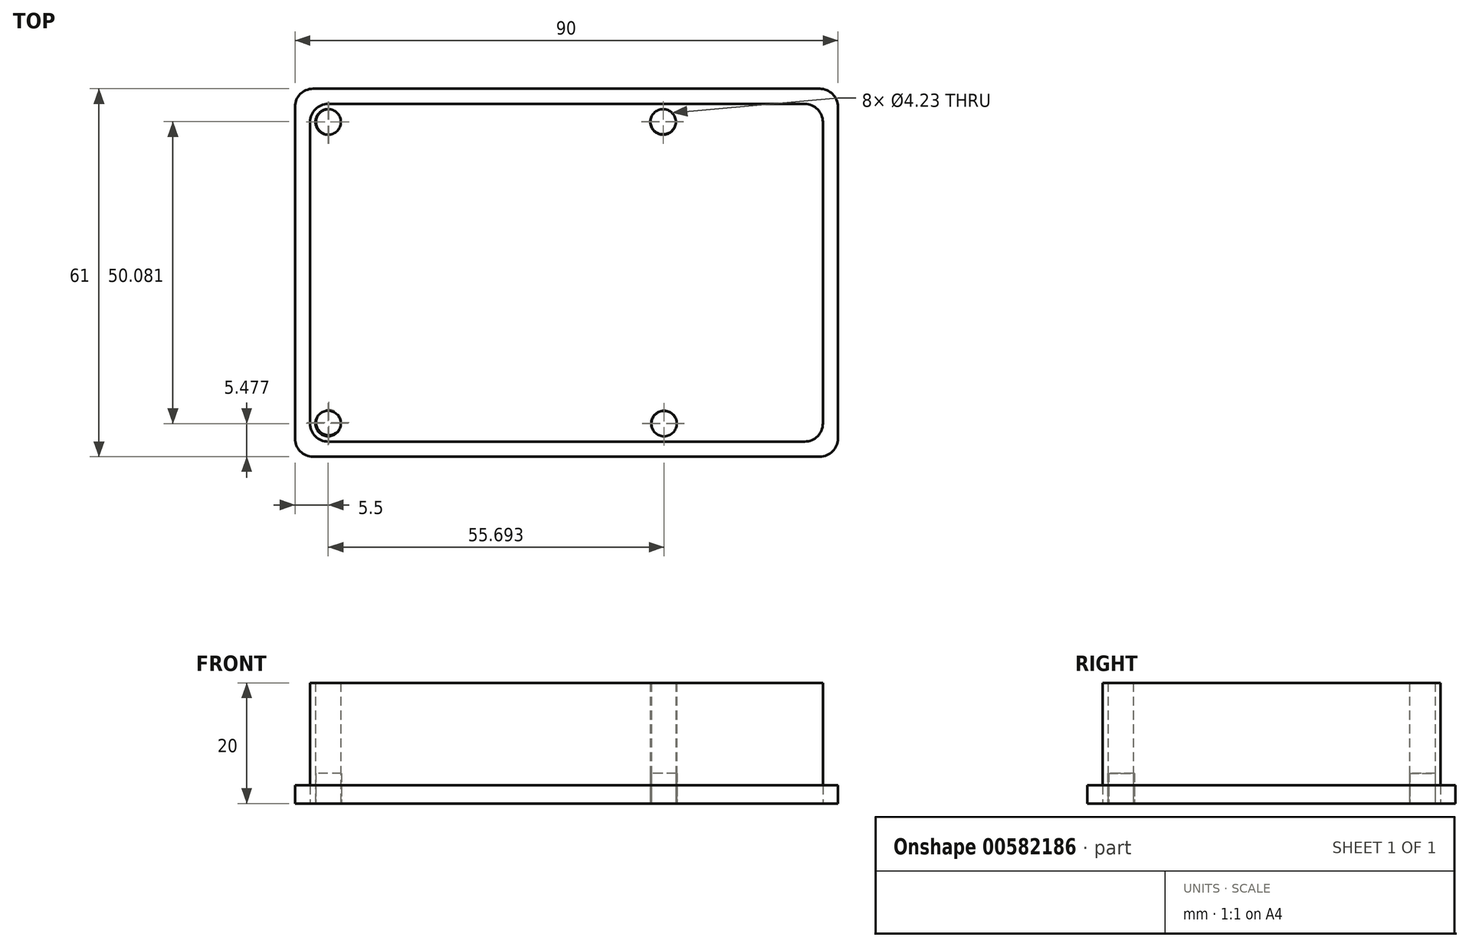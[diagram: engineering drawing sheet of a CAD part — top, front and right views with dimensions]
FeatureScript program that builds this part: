
annotation { "Feature Type Name" : "Feature", "Feature Type Description" : "" }
export const myFeature = defineFeature(function(context is Context, id is Id, definition is map)
    precondition{}
    {
        {
            var Q0;
            Q0=qCreatedBy(makeId("Top.planeOp"),FACE);
            var sketch = newSketch(context, id + "F0", { "sketchPlane" : qUnion([Q0])});
            skLineSegment(sketch, "E0.bottom", {"start": v(-39.5, -28) * mm, "end": v(39.5, -28) * mm});
            skLineSegment(sketch, "E0.top", {"start": v(-39.5, 28) * mm, "end": v(39.5, 28) * mm});
            skLineSegment(sketch, "E0.left", {"start": v(-42.5, -25) * mm, "end": v(-42.5, 25) * mm});
            skLineSegment(sketch, "E0.right", {"start": v(42.5, -25) * mm, "end": v(42.5, 25) * mm});
            skPoint(sketch, "E0.middle", {"position": v(0, 0) * mm});
            skPoint(sketch, "E1.visualSharp", {"position": v(-42.5, -28) * mm});
            skArc(sketch, "E1.filletArc", {"start": v(-42.5, -25) * mm, "mid": v(-41.62, -27.12) * mm, "end": v(-39.5, -28) * mm});
            skPoint(sketch, "E2.visualSharp", {"position": v(-42.5, 28) * mm});
            skArc(sketch, "E2.filletArc", {"start": v(-39.5, 28) * mm, "mid": v(-41.62, 27.12) * mm, "end": v(-42.5, 25) * mm});
            skPoint(sketch, "E3.visualSharp", {"position": v(42.5, 28) * mm});
            skArc(sketch, "E3.filletArc", {"start": v(42.5, 25) * mm, "mid": v(41.62, 27.12) * mm, "end": v(39.5, 28) * mm});
            skPoint(sketch, "E4.visualSharp", {"position": v(42.5, -28) * mm});
            skArc(sketch, "E4.filletArc", {"start": v(39.5, -28) * mm, "mid": v(41.62, -27.12) * mm, "end": v(42.5, -25) * mm});
            skCircle(sketch, "E5", {"center": v(-39.5, -25) * mm, "radius": 2.11 * mm});
            skCircle(sketch, "E6", {"center": v(-39.5, 25) * mm, "radius": 2.11 * mm});
            skCircle(sketch, "E7", {"center": v(16.02, 25) * mm, "radius": 2.11 * mm});
            skCircle(sketch, "E8", {"center": v(16.18, -25) * mm, "radius": 2.11 * mm});
            skSolve(sketch);
        }
        {
            var Q0;
            Q0=makeQuery(id+"F0.imprint","IMPRINT",FACE,{"disambiguationData":[TD([[makeQuery(id+"F0.imprint","IMPRINT",EDGE,{"derivedFrom":sQuery(id+"F0.wireOp",EDGE,"E0.bottom")}),1.0]])]});
            extrude(context, id + "F1", {"entities" : qUnion([Q0]), "depth" : 20 * mm, "offsetDistance" : 25 * mm});
        }
        {
            var Q0;
            Q0=qCreatedBy(makeId("Top.planeOp"),FACE);
            var sketch = newSketch(context, id + "F2", { "sketchPlane" : qUnion([Q0])});
            skLineSegment(sketch, "E9.bottom", {"start": v(42, 30.5) * mm, "end": v(-42, 30.5) * mm});
            skLineSegment(sketch, "E9.top", {"start": v(42, -30.5) * mm, "end": v(-42, -30.5) * mm});
            skLineSegment(sketch, "E9.left", {"start": v(45, 27.5) * mm, "end": v(45, -27.5) * mm});
            skLineSegment(sketch, "E9.right", {"start": v(-45, 27.5) * mm, "end": v(-45, -27.5) * mm});
            skPoint(sketch, "E9.middle", {"position": v(0, 0) * mm});
            skCircle(sketch, "E10", {"center": v(-39.4, -24.82) * mm, "radius": 2.11 * mm});
            skCircle(sketch, "E11", {"center": v(-39.4, 25) * mm, "radius": 2.11 * mm});
            skCircle(sketch, "E12", {"center": v(16.03, 25.06) * mm, "radius": 2.11 * mm});
            skCircle(sketch, "E13", {"center": v(16.2, -25.02) * mm, "radius": 2.11 * mm});
            skPoint(sketch, "E14.visualSharp", {"position": v(45, 30.5) * mm});
            skArc(sketch, "E14.filletArc", {"start": v(45, 27.5) * mm, "mid": v(44.12, 29.62) * mm, "end": v(42, 30.5) * mm});
            skPoint(sketch, "E15.visualSharp", {"position": v(45, -30.5) * mm});
            skArc(sketch, "E15.filletArc", {"start": v(42, -30.5) * mm, "mid": v(44.12, -29.62) * mm, "end": v(45, -27.5) * mm});
            skPoint(sketch, "E16.visualSharp", {"position": v(-45, 30.5) * mm});
            skArc(sketch, "E16.filletArc", {"start": v(-42, 30.5) * mm, "mid": v(-44.12, 29.62) * mm, "end": v(-45, 27.5) * mm});
            skPoint(sketch, "E17.visualSharp", {"position": v(-45, -30.5) * mm});
            skArc(sketch, "E17.filletArc", {"start": v(-45, -27.5) * mm, "mid": v(-44.12, -29.62) * mm, "end": v(-42, -30.5) * mm});
            skSolve(sketch);
        }
        {
            var Q0;
            Q0=makeQuery(id+"F2.imprint","IMPRINT",FACE,{"disambiguationData":[TD([[makeQuery(id+"F2.imprint","IMPRINT",EDGE,{"derivedFrom":sQuery(id+"F2.wireOp",EDGE,"E10")}),1.0]])]});
            var Q1;
            Q1=makeQuery(id+"F2.imprint","IMPRINT",FACE,{"disambiguationData":[TD([[makeQuery(id+"F2.imprint","IMPRINT",EDGE,{"derivedFrom":sQuery(id+"F2.wireOp",EDGE,"E12")}),1.0]])]});
            var Q2;
            Q2=makeQuery(id+"F2.imprint","IMPRINT",FACE,{"disambiguationData":[TD([[makeQuery(id+"F2.imprint","IMPRINT",EDGE,{"derivedFrom":sQuery(id+"F2.wireOp",EDGE,"E13")}),1.0]])]});
            var Q3;
            Q3=makeQuery(id+"F2.imprint","IMPRINT",FACE,{"disambiguationData":[TD([[makeQuery(id+"F2.imprint","IMPRINT",EDGE,{"derivedFrom":sQuery(id+"F2.wireOp",EDGE,"E11")}),1.0]])]});
            extrude(context, id + "F3", {"entities" : qUnion([Q0, Q1, Q2, Q3]), "depth" : 5 * mm, "offsetDistance" : 25 * mm});
        }
        {
            var Q0;
            Q0=makeQuery(id+"F2.imprint","IMPRINT",FACE,{"disambiguationData":[TD([[makeQuery(id+"F2.imprint","IMPRINT",EDGE,{"derivedFrom":sQuery(id+"F2.wireOp",EDGE,"E9.bottom")}),1.0]])]});
            extrude(context, id + "F4", {"entities" : qUnion([Q0]), "depth" : 3 * mm, "offsetDistance" : 25 * mm});
        }
    });
